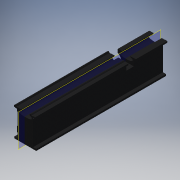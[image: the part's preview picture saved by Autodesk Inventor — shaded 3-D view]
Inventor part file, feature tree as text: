
AUTODESK INVENTOR PART (.ipt)
format: ipt  version: 2016 (Build 200138000, 138)  size: 400,896 bytes
history: native  units: in
note: dims shown in document units (in); Inventor stores cm internally (conversion verified against a paired STEP export)
features: extrude x11, sketch x11, reference x6, plane x3, chamfer x1
ambient origin geometry x8: Origin, YZ Plane, XZ Plane, XY Plane, X Axis, Y Axis, Z Axis, Center Point
bodies: Solid1 (feature_tree)
feature tree (32):
  extrude  "Extrusion1"  TaperAngle=150.0deg  [1 undecoded]
  chamfer  "Chamfer1"  Distance=0.9921in
  plane  "Work Plane3"
  extrude  "Extrusion2"  Depth=0.7874in
  extrude  "Extrusion3"  Depth=0.7874in
  extrude  "Extrusion4"  Depth=0.7874in
  extrude  "Extrusion5"  TaperAngle=120.0deg  [1 undecoded]
  extrude  "Extrusion6"  Depth=0.1575in
  extrude  "Extrusion7"  Depth=0.7874in
  extrude  "Extrusion8"  Depth=0.7874in
  plane  "Work Plane4"
  plane  "Work Plane5"
  extrude  "Extrusion9"  Depth=0.7874in
  extrude  "Extrusion10"  Depth=0.7874in
  extrude  "Extrusion11"  Depth=0.7874in
  sketch  "Sketch1"  dims[d0=0.4331in d1=150.0deg]
  sketch  "Sketch2"  dims[d2=0.3937in]
  sketch  "Sketch3"  dims[d3=0.4606in]
  sketch  "Sketch4"  dims[d4=0.4961in]
  sketch  "Sketch5"  dims[d5=0.962in]
  sketch  "Sketch6"  dims[d6=0.1496in]
  sketch  "Sketch8"  dims[d7=0.4016in]
  sketch  "Sketch9"  dims[d8=0.962in]
  sketch  "Sketch10"  dims[d9=0.126in]
  sketch  "Sketch11"  dims[d10=0.6339in]
  sketch  "Sketch12"  dims[d11=0.0787in d12=0.9921in d13=0.6181in d14=0.5787in d15=0.315in d16=120.0deg d17=0.1575in d18=2.4409in d19=8.0315in d22=3.6299in d24=0.5in d25=1.4252in d26=180.0deg d27=0.0787in d28=0.748in d29=0.0787in d30=0.5197in d31=0.962in d32=0.1811in d33=0.6299in d34=0.962in d35=0.5512in d36=0.5512in d37=90.0deg d38=0.1181in d39=60.0deg d40=0.685in d41=0.8858in d43=5.2953in d44=90.0deg d46=2.185in d47=90.0deg d50=90.0deg d51=1.378in d52=180.0deg d53=0.7087in d54=90.0deg d55=1.378in d57=0.7087in d59=180.0deg d60=0.315in d61=120.0deg d62=2.4409in d63=55.9055in d64=0.0in d65=0.1575in d66=0.0787in d67=45.0deg d68=40.1575in d69=3.2283in d70=3.4528in d71=55.9055in d72=0.0in d73=55.9055in d74=0.0in d75=55.9055in d76=0.0in d77=3.3465in d78=1.2205in d79=1.7323in d80=55.9055in d81=0.0in d82=1.0236in d83=0.0in d84=0.315in d85=0.315in d86=0.7283in d87=0.5512in d88=0.5118in d89=0.3937in d90=0.0in d91=0.315in d92=0.315in d93=6.7717in d94=0.8858in d95=0.5512in d96=0.7874in d97=0.0in d98=0.2756in d99=0.3937in d100=0.0in d101=5.5118in d102=1.9685in d103=0.2756in d104=1.5748in d105=0.0787in d106=0.0in d107=0.7874in d108=0.0in]
  reference  "Reference1"
  reference  "Reference2"
  reference  "Reference3"
  reference  "Reference4"
  reference  "Reference5"
  reference  "Reference6"
note: 2 required parameter values undecoded (feature->parameter linkage not recoverable at this tier; creation-order binding heuristic only, values carry confidence <= 0.55)
